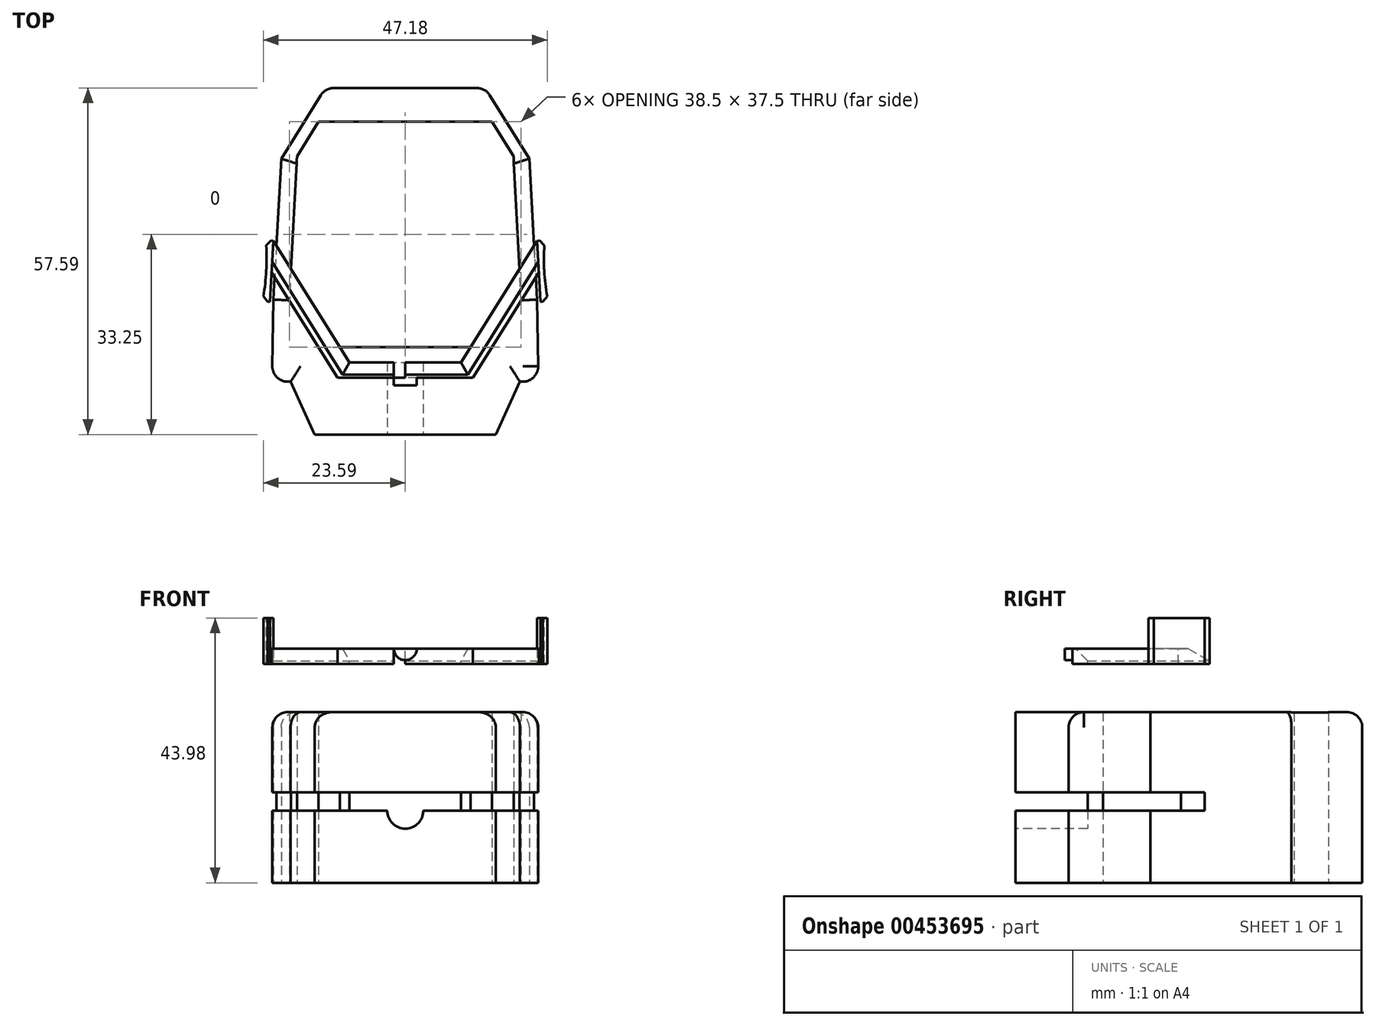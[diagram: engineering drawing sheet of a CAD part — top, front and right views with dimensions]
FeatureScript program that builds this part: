
annotation { "Feature Type Name" : "Feature", "Feature Type Description" : "" }
export const myFeature = defineFeature(function(context is Context, id is Id, definition is map)
    precondition{}
    {
        {
            var Q0;
            Q0=qCreatedBy(makeId("Top.planeOp"),FACE);
            var sketch = newSketch(context, id + "F0", { "sketchPlane" : qUnion([Q0])});
            skLineSegment(sketch, "E0", {"start": v(-14.4, -18.75) * mm, "end": v(14.4, -18.75) * mm});
            skLineSegment(sketch, "E1", {"start": v(14.4, -18.75) * mm, "end": v(19.25, -10.98) * mm});
            skLineSegment(sketch, "E2", {"start": v(19.25, -10.98) * mm, "end": v(18, 12.99) * mm});
            skLineSegment(sketch, "E3", {"start": v(18, 12.99) * mm, "end": v(14.4, 18.75) * mm});
            skLineSegment(sketch, "E4", {"start": v(14.4, 18.75) * mm, "end": v(-14.4, 18.75) * mm});
            skLineSegment(sketch, "E5", {"start": v(-14.4, 18.75) * mm, "end": v(-18, 12.99) * mm});
            skLineSegment(sketch, "E6", {"start": v(-18, 12.99) * mm, "end": v(-19.25, -10.98) * mm});
            skLineSegment(sketch, "E7", {"start": v(-19.25, -10.98) * mm, "end": v(-14.4, -18.75) * mm});
            skLineSegment(sketch, "E8", {"start": v(-15.04, -33.25) * mm, "end": v(15.04, -33.25) * mm});
            skLineSegment(sketch, "E9", {"start": v(22.13, -24.46) * mm, "end": v(21.92, -10.84) * mm});
            skLineSegment(sketch, "E10", {"start": v(13.27, 24.34) * mm, "end": v(-13.27, 24.34) * mm});
            skLineSegment(sketch, "E11", {"start": v(18, 12.99) * mm, "end": v(20.58, 13.12) * mm, "construction": true});
            skLineSegment(sketch, "E12", {"start": v(19.25, -10.98) * mm, "end": v(21.92, -10.84) * mm, "construction": true});
            skLineSegment(sketch, "E13", {"start": v(20.58, 13.12) * mm, "end": v(21.92, -10.84) * mm});
            skLineSegment(sketch, "E14", {"start": v(13.27, 24.34) * mm, "end": v(20.61, 12.6) * mm});
            skLineSegment(sketch, "E15.MirrorCS", {"start": v(-22.13, -24.46) * mm, "end": v(-21.92, -10.84) * mm});
            skLineSegment(sketch, "E16.MirrorCS", {"start": v(-13.27, 24.34) * mm, "end": v(-20.61, 12.6) * mm});
            skLineSegment(sketch, "E17.MirrorCS", {"start": v(-20.58, 13.12) * mm, "end": v(-21.92, -10.84) * mm});
            skLineSegment(sketch, "E18", {"start": v(19.05, -24.46) * mm, "end": v(22.13, -24.46) * mm});
            skLineSegment(sketch, "E19.MirrorCS", {"start": v(-19.05, -24.46) * mm, "end": v(-22.13, -24.46) * mm});
            skLineSegment(sketch, "E20", {"start": v(15.04, -33.25) * mm, "end": v(19.05, -24.46) * mm});
            skLineSegment(sketch, "E21", {"start": v(-15.04, -33.25) * mm, "end": v(-19.05, -24.46) * mm});
            skSolve(sketch);
        }
        {
            var Q0;
            Q0=makeQuery(id+"F0.imprint","IMPRINT",FACE,{"disambiguationData":[TD([[makeQuery(id+"F0.imprint","IMPRINT",EDGE,{"derivedFrom":sQuery(id+"F0.wireOp",EDGE,"E0")}),-1.0]])]});
            extrude(context, id + "F1", {"entities" : qUnion([Q0]), "depth" : 28.35 * mm});
        }
        {
            var Q0;
            Q0=qCreatedBy(makeId("Top.planeOp"),FACE);
            cPlane(context, id + "F2", {"entities" : qUnion([Q0]), "cplaneType" : CPlaneType.OFFSET, "offset" : 13.5 * mm, "width" : 150 * mm, "height" : 150 * mm});
        }
        {
            var Q0;
            Q0=qCreatedBy(id+"F2.planeOp",FACE);
            var sketch = newSketch(context, id + "F3", { "sketchPlane" : qUnion([Q0])});
            skLineSegment(sketch, "E22.0", {"start": v(-19.25, -10.98) * mm, "end": v(-14.4, -18.75) * mm, "construction": true});
            skLineSegment(sketch, "E23.0", {"start": v(-15.04, -33.25) * mm, "end": v(15.04, -33.25) * mm, "construction": true});
            skLineSegment(sketch, "E24", {"start": v(-24, -0.55) * mm, "end": v(-3.56, -33.25) * mm, "construction": true});
            skLineSegment(sketch, "E25", {"start": v(-10.75, -21.75) * mm, "end": v(-12.02, -22.54) * mm});
            skLineSegment(sketch, "E26", {"start": v(-12.02, -22.54) * mm, "end": v(-25.27, -1.34) * mm});
            skLineSegment(sketch, "E27", {"start": v(-10.75, -21.75) * mm, "end": v(-24, -0.55) * mm});
            skLineSegment(sketch, "E28", {"start": v(-25.27, -1.34) * mm, "end": v(-24, -0.55) * mm});
            skLineSegment(sketch, "E29.0.0", {"start": v(13.27, 24.34) * mm, "end": v(-13.27, 24.34) * mm});
            skLineSegment(sketch, "E29.0.1", {"start": v(-13.27, 24.34) * mm, "end": v(-20.61, 12.6) * mm});
            skLineSegment(sketch, "E29.0.2", {"start": v(-20.61, 12.6) * mm, "end": v(-21.92, -10.84) * mm});
            skLineSegment(sketch, "E29.0.3", {"start": v(-21.92, -10.84) * mm, "end": v(-22.13, -24.46) * mm});
            skLineSegment(sketch, "E29.0.4", {"start": v(-22.13, -24.46) * mm, "end": v(-19.05, -24.46) * mm});
            skLineSegment(sketch, "E29.0.5", {"start": v(-19.05, -24.46) * mm, "end": v(-15.04, -33.25) * mm});
            skLineSegment(sketch, "E29.0.6", {"start": v(-15.04, -33.25) * mm, "end": v(15.04, -33.25) * mm});
            skLineSegment(sketch, "E29.0.7", {"start": v(15.04, -33.25) * mm, "end": v(19.05, -24.46) * mm});
            skLineSegment(sketch, "E29.0.8", {"start": v(19.05, -24.46) * mm, "end": v(22.13, -24.46) * mm});
            skLineSegment(sketch, "E29.0.9", {"start": v(22.13, -24.46) * mm, "end": v(21.92, -10.84) * mm});
            skLineSegment(sketch, "E29.0.10", {"start": v(21.92, -10.84) * mm, "end": v(20.61, 12.6) * mm});
            skLineSegment(sketch, "E29.0.11", {"start": v(20.61, 12.6) * mm, "end": v(13.27, 24.34) * mm});
            skLineSegment(sketch, "E30.MirrorCS", {"start": v(12.02, -22.54) * mm, "end": v(25.27, -1.34) * mm});
            skLineSegment(sketch, "E31", {"start": v(-12.8, -21.29) * mm, "end": v(-11.04, -21.29) * mm});
            skLineSegment(sketch, "E32", {"start": v(-9.27, -21.29) * mm, "end": v(-21.42, -1.86) * mm});
            skLineSegment(sketch, "E33.MirrorCS", {"start": v(9.27, -21.29) * mm, "end": v(21.42, -1.86) * mm});
            skLineSegment(sketch, "E34.trimOffspring", {"start": v(-9.27, -21.29) * mm, "end": v(9.27, -21.29) * mm});
            skSolve(sketch);
        }
        {
            var Q0;
            Q0=makeQuery(id+"F1.opExtrude","CAP_EDGE",EDGE,{"disambiguationData":[OSD([sQuery(id+"F0.wireOp",EDGE,"E21")])],"isStart":false});
            var Q1;
            Q1=makeQuery(id+"F1.opExtrude","CAP_EDGE",EDGE,{"disambiguationData":[OSD([sQuery(id+"F0.wireOp",EDGE,"E19.MirrorCS")])],"isStart":false});
            var Q2;
            Q2=makeQuery(id+"F1.opExtrude","CAP_EDGE",EDGE,{"disambiguationData":[OSD([sQuery(id+"F0.wireOp",EDGE,"E17.MirrorCS")])],"isStart":false});
            var Q3;
            Q3=makeQuery(id+"F1.opExtrude","CAP_EDGE",EDGE,{"disambiguationData":[OSD([sQuery(id+"F0.wireOp",EDGE,"E15.MirrorCS")])],"isStart":false});
            var Q4;
            Q4=makeQuery(id+"F1.opExtrude","CAP_EDGE",EDGE,{"disambiguationData":[OSD([sQuery(id+"F0.wireOp",EDGE,"E16.MirrorCS")])],"isStart":false});
            var Q5;
            Q5=makeQuery(id+"F1.opExtrude","CAP_EDGE",EDGE,{"disambiguationData":[OSD([sQuery(id+"F0.wireOp",EDGE,"E10")])],"isStart":false});
            var Q6;
            Q6=makeQuery(id+"F1.opExtrude","CAP_EDGE",EDGE,{"disambiguationData":[OSD([sQuery(id+"F0.wireOp",EDGE,"E14")])],"isStart":false});
            var Q7;
            Q7=makeQuery(id+"F1.opExtrude","CAP_EDGE",EDGE,{"disambiguationData":[OSD([sQuery(id+"F0.wireOp",EDGE,"E13")])],"isStart":false});
            var Q8;
            Q8=makeQuery(id+"F1.opExtrude","CAP_EDGE",EDGE,{"disambiguationData":[OSD([sQuery(id+"F0.wireOp",EDGE,"E9")])],"isStart":false});
            var Q9;
            Q9=makeQuery(id+"F1.opExtrude","CAP_EDGE",EDGE,{"disambiguationData":[OSD([sQuery(id+"F0.wireOp",EDGE,"E18")])],"isStart":false});
            var Q10;
            Q10=makeQuery(id+"F1.opExtrude","CAP_EDGE",EDGE,{"disambiguationData":[OSD([sQuery(id+"F0.wireOp",EDGE,"E20")])],"isStart":false});
            fillet(context, id + "F4", {"entities" : qUnion([Q0, Q1, Q2, Q3, Q4, Q5, Q6, Q7, Q8, Q9, Q10]), "radius" : 2.54 * mm, "tangentPropagation" : true, "allowEdgeOverflow" : false});
        }
        {
            var Q0;
            Q0=makeQuery(id+"F4.opFillet","BLEND_EDGE",EDGE,{"blendedFrom":[makeQuery(id+"F1.opExtrude","CAP_EDGE",EDGE,{"disambiguationData":[OSD([sQuery(id+"F0.wireOp",EDGE,"E9")])],"isStart":false}),makeQuery(id+"F1.opExtrude","CAP_EDGE",EDGE,{"disambiguationData":[OSD([sQuery(id+"F0.wireOp",EDGE,"E18")])],"isStart":false})],"blendedInto":[]});
            var Q1;
            Q1=makeQuery(id+"F4.opFillet","BLEND_EDGE",EDGE,{"blendedFrom":[makeQuery(id+"F1.opExtrude","CAP_EDGE",EDGE,{"disambiguationData":[OSD([sQuery(id+"F0.wireOp",EDGE,"E15.MirrorCS")])],"isStart":false}),makeQuery(id+"F1.opExtrude","CAP_EDGE",EDGE,{"disambiguationData":[OSD([sQuery(id+"F0.wireOp",EDGE,"E19.MirrorCS")])],"isStart":false})],"blendedInto":[]});
            var Q2;
            Q2=makeQuery(id+"F4.opFillet","BLEND_EDGE",EDGE,{"blendedFrom":[makeQuery(id+"F1.opExtrude","CAP_EDGE",EDGE,{"disambiguationData":[OSD([sQuery(id+"F0.wireOp",EDGE,"E10")])],"isStart":false}),makeQuery(id+"F1.opExtrude","CAP_EDGE",EDGE,{"disambiguationData":[OSD([sQuery(id+"F0.wireOp",EDGE,"E16.MirrorCS")])],"isStart":false})],"blendedInto":[]});
            var Q3;
            Q3=makeQuery(id+"F4.opFillet","BLEND_EDGE",EDGE,{"blendedFrom":[makeQuery(id+"F1.opExtrude","CAP_EDGE",EDGE,{"disambiguationData":[OSD([sQuery(id+"F0.wireOp",EDGE,"E10")])],"isStart":false}),makeQuery(id+"F1.opExtrude","CAP_EDGE",EDGE,{"disambiguationData":[OSD([sQuery(id+"F0.wireOp",EDGE,"E14")])],"isStart":false})],"blendedInto":[]});
            fillet(context, id + "F5", {"entities" : qUnion([Q0, Q1, Q2, Q3]), "radius" : 2.54 * mm, "tangentPropagation" : true, "allowEdgeOverflow" : false});
        }
        {
            var Q0;
            {var subQ0=sQuery(id+"F3.wireOp",EDGE,"E25");Q0=makeQuery(id+"F3.imprint","IMPRINT",FACE,{"disambiguationData":[TD([[makeQuery(id+"F3.imprint","IMPRINT",EDGE,{"derivedFrom":subQ0}),1.0]])]});}
            var Q1;
            {var subQ0=sQuery(id+"F3.wireOp",EDGE,"E25");Q1=makeQuery(id+"F3.imprint","IMPRINT",FACE,{"disambiguationData":[TD([[makeQuery(id+"F3.imprint","IMPRINT",EDGE,{"derivedFrom":subQ0}),-1.0]])]});}
            var Q2;
            {var subQ0=sQuery(id+"F3.wireOp",EDGE,"E31");var subQ1=sQuery(id+"F3.wireOp",EDGE,"E26");var subQ2=makeQuery(id+"F3.imprint","INTERSECT",VERTEX,{"derivedFrom":[subQ1,subQ0]});Q2=makeQuery(id+"F3.imprint","IMPRINT",FACE,{"disambiguationData":[TD([[makeQuery(id+"F3.imprint","IMPRINT",EDGE,{"disambiguationData":[TD([[subQ2,-1.0]])],"derivedFrom":subQ1}),-1.0]])]});}
            extrude(context, id + "F6", {"entities" : qUnion([Q0, Q1, Q2]), "operationType" : NewBodyOperationType.REMOVE, "depth" : 1.5 * mm, "hasSecondDirection" : true, "secondDirectionOppositeDirection" : true, "secondDirectionDepth" : 1.5 * mm});
        }
        {
            var Q0;
            {var subQ2=sQuery(id+"F0.wireOp",EDGE,"E8");Q0=makeQuery(id+"F6.boolean.opBoolean","SPLIT",FACE,{"disambiguationData":[TD([makeQuery(id+"F6.opExtrude","CAP_FACE",FACE,{"disambiguationData":[OSD([sQuery(id+"F3.wireOp",EDGE,"E29.0.2"),sQuery(id+"F3.wireOp",EDGE,"E29.0.3"),sQuery(id+"F3.wireOp",EDGE,"E29.0.4"),sQuery(id+"F3.wireOp",EDGE,"E29.0.5"),sQuery(id+"F3.wireOp",EDGE,"E29.0.6"),sQuery(id+"F3.wireOp",EDGE,"E29.0.7"),sQuery(id+"F3.wireOp",EDGE,"E29.0.8"),sQuery(id+"F3.wireOp",EDGE,"E29.0.9"),sQuery(id+"F3.wireOp",EDGE,"E29.0.10"),sQuery(id+"F3.wireOp",EDGE,"E32"),sQuery(id+"F3.wireOp",EDGE,"E33.MirrorCS"),sQuery(id+"F3.wireOp",EDGE,"E34.trimOffspring")])],"isStart":true})])],"derivedFrom":makeQuery(id+"F1.opExtrude","SWEPT_FACE",FACE,{"disambiguationData":[OSD([subQ2])]})});}
            var sketch = newSketch(context, id + "F7", { "sketchPlane" : qUnion([Q0])});
            skPoint(sketch, "E35.0", {"position": v(0, 15) * mm});
            skCircle(sketch, "E36", {"center": v(0, 12) * mm, "radius": 3 * mm});
            skSolve(sketch);
        }
        {
            var Q0;
            {var subQ0=sQuery(id+"F7.wireOp",EDGE,"E36");var subQ1=makeQuery(id+"F6.boolean.opBoolean","COPY",EDGE,{"derivedFrom":makeQuery(id+"F6.opExtrude","CAP_EDGE",EDGE,{"disambiguationData":[OSD([sQuery(id+"F3.wireOp",EDGE,"E29.0.6")])],"isStart":true})});var subQ2=makeQuery(id+"F7.imprint","INTERSECT",VERTEX,{"disambiguationData":[OD(0.0)],"derivedFrom":[subQ1,subQ0]});Q0=makeQuery(id+"F7.imprint","IMPRINT",FACE,{"disambiguationData":[TD([[makeQuery(id+"F7.imprint","IMPRINT",EDGE,{"disambiguationData":[TD([[subQ2,-1.0]])],"derivedFrom":subQ0}),1.0]])]});}
            extrude(context, id + "F8", {"entities" : qUnion([Q0]), "operationType" : NewBodyOperationType.REMOVE, "oppositeDirection" : true, "depth" : 11.96 * mm});
        }
        {
            var Q0;
            Q0=qCreatedBy(id+"F2.planeOp",FACE);
            cPlane(context, id + "F9", {"entities" : qUnion([Q0]), "cplaneType" : CPlaneType.OFFSET, "offset" : 25.4 * mm, "width" : 152.4 * mm, "height" : 152.4 * mm});
        }
        {
            var Q0;
            Q0=qCreatedBy(id+"F9.planeOp",FACE);
            var sketch = newSketch(context, id + "F10", { "sketchPlane" : qUnion([Q0])});
            skLineSegment(sketch, "E37.0.0", {"start": v(21.92, -10.84) * mm, "end": v(21.42, -1.86) * mm});
            skLineSegment(sketch, "E37.0.1", {"start": v(21.42, -1.86) * mm, "end": v(9.27, -21.29) * mm});
            skLineSegment(sketch, "E37.0.2", {"start": v(9.27, -21.29) * mm, "end": v(-9.27, -21.29) * mm});
            skLineSegment(sketch, "E37.0.3", {"start": v(-9.27, -21.29) * mm, "end": v(-21.42, -1.86) * mm});
            skLineSegment(sketch, "E37.0.4", {"start": v(-21.42, -1.86) * mm, "end": v(-21.56, -4.45) * mm});
            skLineSegment(sketch, "E37.0.10", {"start": v(-21.7, -7.05) * mm, "end": v(-21.92, -10.84) * mm});
            skLineSegment(sketch, "E37.0.11", {"start": v(-21.92, -10.84) * mm, "end": v(-22.13, -24.46) * mm});
            skLineSegment(sketch, "E37.0.12", {"start": v(-22.13, -24.46) * mm, "end": v(-19.05, -24.46) * mm});
            skLineSegment(sketch, "E37.0.13", {"start": v(-19.05, -24.46) * mm, "end": v(-15.04, -33.25) * mm});
            skLineSegment(sketch, "E37.0.14", {"start": v(-15.04, -33.25) * mm, "end": v(15.04, -33.25) * mm});
            skLineSegment(sketch, "E37.0.15", {"start": v(15.04, -33.25) * mm, "end": v(19.05, -24.46) * mm});
            skLineSegment(sketch, "E37.0.16", {"start": v(19.05, -24.46) * mm, "end": v(22.13, -24.46) * mm});
            skLineSegment(sketch, "E37.0.17", {"start": v(22.13, -24.46) * mm, "end": v(21.92, -10.84) * mm});
            skLineSegment(sketch, "E38.0", {"start": v(-21.42, -1.86) * mm, "end": v(-21.92, -10.84) * mm});
            skPoint(sketch, "E39.orphan", {"position": v(-20.61, 12.6) * mm});
            skPoint(sketch, "E37.0.6.end.orphan", {"position": v(-10.75, -21.75) * mm});
            skPoint(sketch, "E37.0.6.start.orphan", {"position": v(-11.04, -21.3) * mm});
            skPoint(sketch, "E37.0.8.start.orphan", {"position": v(-12.02, -22.54) * mm});
            skPoint(sketch, "E37.0.9.start.orphan", {"position": v(-12.8, -21.29) * mm});
            skLineSegment(sketch, "E40", {"start": v(-21.7, -7.05) * mm, "end": v(-9.27, -26.95) * mm});
            skPoint(sketch, "E41.endSnap0", {"position": v(0, -21.29) * mm});
            skLineSegment(sketch, "E42", {"start": v(-11.22, -23.83) * mm, "end": v(0, -23.83) * mm});
            skLineSegment(sketch, "E43.bottom", {"start": v(-1.9, -21.29) * mm, "end": v(0, -21.29) * mm});
            skLineSegment(sketch, "E43.top", {"start": v(-1.9, -25.1) * mm, "end": v(0, -25.1) * mm});
            skLineSegment(sketch, "E43.left", {"start": v(-1.9, -21.29) * mm, "end": v(-1.9, -25.1) * mm});
            skLineSegment(sketch, "E43.right", {"start": v(0, -21.29) * mm, "end": v(0, -25.1) * mm});
            skLineSegment(sketch, "E44", {"start": v(-21.42, -1.86) * mm, "end": v(-21.92, -1.05) * mm});
            skLineSegment(sketch, "E45", {"start": v(-21.7, -7.05) * mm, "end": v(-22.2, -6.25) * mm});
            skLineSegment(sketch, "E46", {"start": v(-21.92, -1.05) * mm, "end": v(-22.2, -6.25) * mm});
            skLineSegment(sketch, "E47", {"start": v(-21.92, -1.05) * mm, "end": v(-23.18, -0.98) * mm});
            skLineSegment(sketch, "E48", {"start": v(-23.18, -0.98) * mm, "end": v(-23.75, -11.13) * mm});
            skLineSegment(sketch, "E49", {"start": v(-22.2, -6.25) * mm, "end": v(-22.48, -11.2) * mm});
            skLineSegment(sketch, "E50", {"start": v(-23.75, -11.13) * mm, "end": v(-22.48, -11.2) * mm});
            skArc(sketch, "E51", {"start": v(-23.75, -11.13) * mm, "mid": v(-23.1, -6.08) * mm, "end": v(-23.18, -0.98) * mm});
            skLineSegment(sketch, "E52.MirrorCS", {"start": v(11.22, -23.83) * mm, "end": v(0, -23.83) * mm});
            skLineSegment(sketch, "E53.MirrorCS", {"start": v(21.7, -7.05) * mm, "end": v(9.27, -26.95) * mm});
            skLineSegment(sketch, "E54.MirrorCS", {"start": v(21.7, -7.05) * mm, "end": v(22.2, -6.25) * mm});
            skLineSegment(sketch, "E55.MirrorCS", {"start": v(22.2, -6.25) * mm, "end": v(22.48, -11.2) * mm});
            skLineSegment(sketch, "E56.MirrorCS", {"start": v(23.75, -11.13) * mm, "end": v(22.48, -11.2) * mm});
            skArc(sketch, "E57.MirrorCS", {"start": v(23.75, -11.13) * mm, "mid": v(23.1, -6.08) * mm, "end": v(23.18, -0.98) * mm});
            skLineSegment(sketch, "E58.MirrorCS", {"start": v(21.92, -1.05) * mm, "end": v(23.18, -0.98) * mm});
            skLineSegment(sketch, "E59.MirrorCS", {"start": v(21.42, -1.86) * mm, "end": v(21.92, -1.05) * mm});
            skLineSegment(sketch, "E60", {"start": v(22.2, -6.25) * mm, "end": v(21.92, -1.05) * mm});
            skSolve(sketch);
        }
        {
            var Q0;
            {var subQ1=sQuery(id+"F10.wireOp",EDGE,"E44");Q0=makeQuery(id+"F10.imprint","IMPRINT",FACE,{"disambiguationData":[TD([[makeQuery(id+"F10.imprint","IMPRINT",EDGE,{"derivedFrom":subQ1}),1.0]])]});}
            var Q1;
            {var subQ1=sQuery(id+"F10.wireOp",EDGE,"E37.0.3");Q1=makeQuery(id+"F10.imprint","IMPRINT",FACE,{"disambiguationData":[TD([[makeQuery(id+"F10.imprint","IMPRINT",EDGE,{"derivedFrom":subQ1}),1.0]])]});}
            var Q2;
            {var subQ5=sQuery(id+"F10.wireOp",EDGE,"E43.bottom");Q2=makeQuery(id+"F10.imprint","IMPRINT",FACE,{"disambiguationData":[TD([[makeQuery(id+"F10.imprint","IMPRINT",EDGE,{"derivedFrom":subQ5}),-1.0]])]});}
            var Q3;
            {var subQ4=sQuery(id+"F10.wireOp",EDGE,"E37.0.1");Q3=makeQuery(id+"F10.imprint","IMPRINT",FACE,{"disambiguationData":[TD([[makeQuery(id+"F10.imprint","IMPRINT",EDGE,{"derivedFrom":subQ4}),1.0]])]});}
            var Q4;
            {var subQ0=sQuery(id+"F10.wireOp",EDGE,"E54.MirrorCS");Q4=makeQuery(id+"F10.imprint","IMPRINT",FACE,{"disambiguationData":[TD([[makeQuery(id+"F10.imprint","IMPRINT",EDGE,{"derivedFrom":subQ0}),1.0]])]});}
            var Q5;
            Q5=makeQuery(id+"F10.imprint","IMPRINT",FACE,{"disambiguationData":[TD([[makeQuery(id+"F10.imprint","IMPRINT",EDGE,{"derivedFrom":sQuery(id+"F10.wireOp",EDGE,"E46")}),-1.0]])]});
            var Q6;
            Q6=makeQuery(id+"F10.imprint","IMPRINT",FACE,{"disambiguationData":[TD([[makeQuery(id+"F10.imprint","IMPRINT",EDGE,{"derivedFrom":sQuery(id+"F10.wireOp",EDGE,"E55.MirrorCS")}),1.0]])]});
            extrude(context, id + "F11", {"entities" : qUnion([Q0, Q1, Q2, Q3, Q4, Q5, Q6]), "oppositeDirection" : true, "depth" : 2.54 * mm});
        }
        {
            var Q0;
            Q0=makeQuery(id+"F10.imprint","IMPRINT",FACE,{"disambiguationData":[TD([[makeQuery(id+"F10.imprint","IMPRINT",EDGE,{"derivedFrom":sQuery(id+"F10.wireOp",EDGE,"E46")}),-1.0]])]});
            var Q1;
            Q1=makeQuery(id+"F10.imprint","IMPRINT",FACE,{"disambiguationData":[TD([[makeQuery(id+"F10.imprint","IMPRINT",EDGE,{"derivedFrom":sQuery(id+"F10.wireOp",EDGE,"E55.MirrorCS")}),1.0]])]});
            extrude(context, id + "F12", {"entities" : qUnion([Q0, Q1]), "operationType" : NewBodyOperationType.ADD, "depth" : 5.08 * mm});
        }
        {
            var Q0;
            {var subQ5=sQuery(id+"F10.wireOp",EDGE,"E43.top");Q0=makeQuery(id+"F10.imprint","IMPRINT",FACE,{"disambiguationData":[TD([[makeQuery(id+"F10.imprint","IMPRINT",EDGE,{"derivedFrom":subQ5}),1.0]])]});}
            var Q1;
            Q1=sQuery(id+"F10.wireOp",EDGE,"E43.right");
            revolve(context, id + "F13", {"operationType" : NewBodyOperationType.ADD, "entities" : qUnion([Q0]), "axis" : qUnion([Q1]), "revolveType" : RevolveType.ONE_DIRECTION, "angle" : 180 * degree});
        }
        {
            var Q0;
            Q0=makeQuery(id+"F12.opExtrude","SWEPT_EDGE",EDGE,{"disambiguationData":[OSD([sQuery(id+"F10.wireOp",EDGE,"E57.MirrorCS"),sQuery(id+"F10.wireOp",EDGE,"E58.MirrorCS")])]});
            var Q1;
            Q1=makeQuery(id+"F12.opExtrude","SWEPT_EDGE",EDGE,{"disambiguationData":[OSD([sQuery(id+"F10.wireOp",EDGE,"E56.MirrorCS"),sQuery(id+"F10.wireOp",EDGE,"E57.MirrorCS")])]});
            var Q2;
            Q2=makeQuery(id+"F12.opExtrude","SWEPT_EDGE",EDGE,{"disambiguationData":[OSD([sQuery(id+"F10.wireOp",EDGE,"E47"),sQuery(id+"F10.wireOp",EDGE,"E48"),sQuery(id+"F10.wireOp",EDGE,"E51")])]});
            var Q3;
            Q3=makeQuery(id+"F12.opExtrude","SWEPT_EDGE",EDGE,{"disambiguationData":[OSD([sQuery(id+"F10.wireOp",EDGE,"E48"),sQuery(id+"F10.wireOp",EDGE,"E50"),sQuery(id+"F10.wireOp",EDGE,"E51")])]});
            chamfer(context, id + "F14", {"entities" : qUnion([Q0, Q1, Q2, Q3]), "width" : 0.76 * mm, "tangentPropagation" : true});
        }
        {
            var Q0;
            Q0=makeQuery(id+"F11.opExtrude","CAP_EDGE",EDGE,{"disambiguationData":[OSD([sQuery(id+"F10.wireOp",EDGE,"E37.0.3"),sQuery(id+"F10.wireOp",EDGE,"E44")])],"isStart":true});
            var Q1;
            Q1=makeQuery(id+"F11.opExtrude","CAP_EDGE",EDGE,{"disambiguationData":[OSD([sQuery(id+"F10.wireOp",EDGE,"E37.0.2"),sQuery(id+"F10.wireOp",EDGE,"E43.bottom")])],"isStart":true});
            var Q2;
            Q2=makeQuery(id+"F11.opExtrude","CAP_EDGE",EDGE,{"disambiguationData":[OSD([sQuery(id+"F10.wireOp",EDGE,"E37.0.1"),sQuery(id+"F10.wireOp",EDGE,"E59.MirrorCS")])],"isStart":true});
            chamfer(context, id + "F15", {"entities" : qUnion([Q0, Q1, Q2]), "chamferType" : ChamferType.TWO_OFFSETS, "width1" : 2.03 * mm, "oppositeDirection" : false, "width2" : 2.03 * mm, "tangentPropagation" : true});
        }
    });
